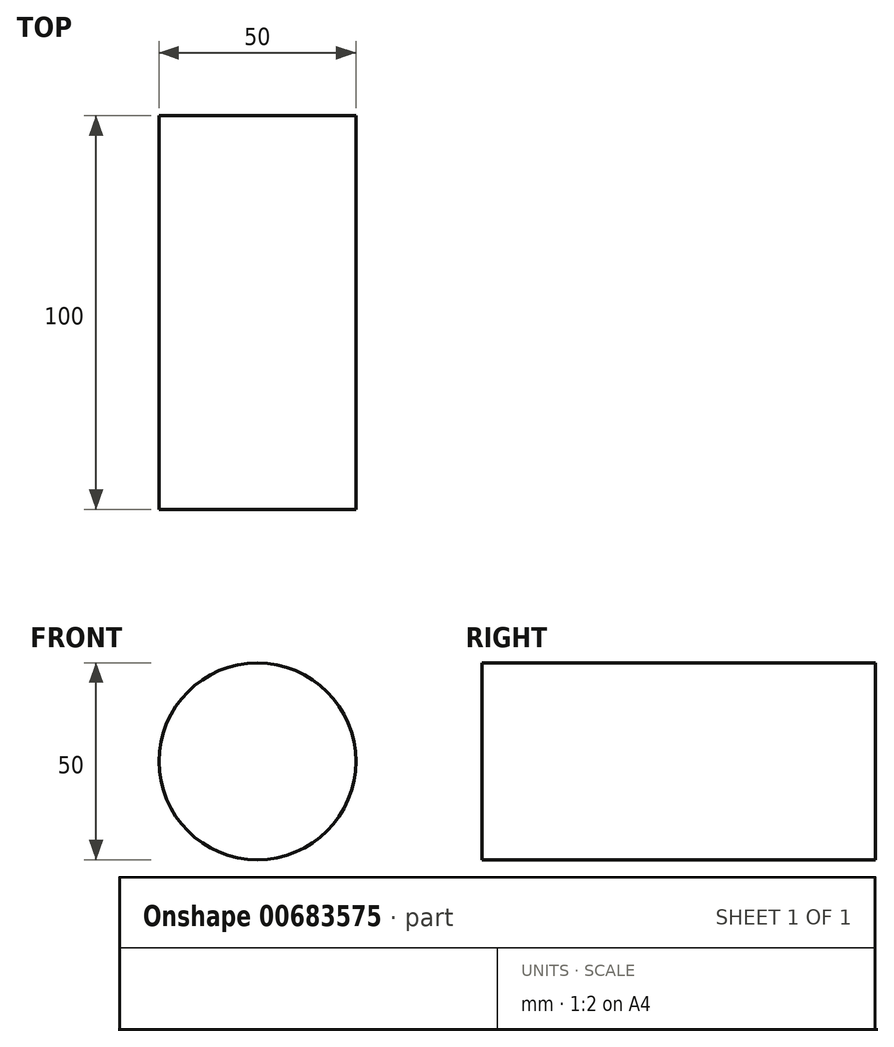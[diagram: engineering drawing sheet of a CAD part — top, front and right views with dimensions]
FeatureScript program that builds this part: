
annotation { "Feature Type Name" : "Feature", "Feature Type Description" : "" }
export const myFeature = defineFeature(function(context is Context, id is Id, definition is map)
    precondition{}
    {
        {
            var Q0;
            Q0=qCreatedBy(makeId("Front.planeOp"),FACE);
            var sketch = newSketch(context, id + "F0", { "sketchPlane" : qUnion([Q0])});
            skCircle(sketch, "E0", {"center": v(0, 0) * mm, "radius": 25 * mm});
            skSolve(sketch);
        }
        {
            var Q0;
            Q0 = qSketchRegion(id + "F0", true);
            extrude(context, id + "F1", {"entities" : qUnion([Q0]), "depth" : 100 * mm, "offsetDistance" : 25 * mm});
        }
    });
